# Revit family: LAMP_SHOT LED G2
name_source: partatom
category: Modelos genéricos
revit_build: Autodesk Revit 2015 (Build: 20140606_1530(x64)
units: mm (PartAtom-declared; Revit-internal decimal feet)

## types (20) — shared parameters
CRI = 80
Comentarios de tipo = Availability of tilting between -50º and 230º when placed in a project.
Elevación por defecto = 1219 mm
Fabricante = LAMP
Gear = Electronic
IEE = A+
Installation instructions = https://www.lamp.es
Insulation class = I
Lamp = HIGH POWER LED
Last update = 12/06/2019
MacAdam = 3
Manufacturer URL = http://www.lamp.es
Manufacturer country = Spain
Manufacturer name = LAMP
Model explanation = Availability of tilting between -50º and 230º when placed in a project.
Power Supply = 220-240V 50-60Hz
Product URL = http://www.lamp.es
Product datasheet = http://www.lamp.es
Protection rating = IP65 / IK05
Type = HI POWER NICHIA

## per-type parameters (varying)
| type | Descripción | Efficacy | Finish | Initial color | Initial intensity | LED Lifetime | Luminaire type | Material lira | Modelo | Photometric web file | Plum | Power | Product code | Weight |
| 3850LM 4000 STREET ANT | SHOT G2 5000 STREET 80 NW ANT | 94 lm/W | Textured anthracite grey | 4000 K | 3850 lm | 60.000 L90 B10 | Outdoor - Spotlight | LAMP_Aluminio Shot Antracita | SH250ST840NA | Cabeza Shot g2 : 3850LM 4000 STREET ANT | 41 W | 37 W | SH250ST840NA | 6.43 kg |
| 3850LM 4000 STREET GR | SHOT G2 5000 STREET 80 NW GR | 94 lm/W | Texturised grey | 4000 K | 3850 lm | 60.000 L90 B10 | Outdoor - Spotlight | LAMP_Aluminio Shot | SH250ST840NG | Cabeza Shot g2 : 3850LM 4000 STREET GR | 41 W | 37 W | SH250ST840NG | 6.43 kg |
| 4112LM 3000 MEDIUM FLOOD ANT | SHOT G2 5000 MFL 80 WW ANT | 100 lm/W | Textured anthracite grey | 3000 K | 4112 lm | 60.000 L90 B10 | Outdoor - Spotlight | LAMP_Aluminio Shot Antracita | SH250MF830NA | Cabeza Shot g2 : 4112LM 3000 MEDIUM FLOOD ANT | 41 W | 37 W | SH250MF830NA | 6.38 kg |
| 4112LM 3000 MEDIUM FLOOD GR | SHOT G2 5000 MFL 80 WW GR | 100 lm/W | Texturised grey | 3000 K | 4112 lm | 60.000 L90 B10 | Outdoor - Spotlight | LAMP_Aluminio Shot | SH250MF830NG | Cabeza Shot g2 : 4112LM 3000 MEDIUM FLOOD GR | 41 W | 37 W | SH250MF830NG | 6.38 kg |
| 4112LM 4000 MEDIUM FLOOD ANT | SHOT G2 5000 MFL 80 NW ANT | 100 lm/W | Textured anthracite grey | 4000 K | 4112 lm | 60.000 L90 B10 | Outdoor - Spotlight | LAMP_Aluminio Shot Antracita | SH250MF840NA | Cabeza Shot g2 : 4112LM 4000 MEDIUM FLOOD ANT | 41 W | 37 W | SH250MF840NA | 6.38 kg |
| 4112LM 4000 MEDIUM FLOOD GR | SHOT G2 5000 MFL 80 NW GR | 100 lm/W | Texturised grey | 4000 K | 4112 lm | 60.000 L90 B10 | Outdoor - Spotlight | LAMP_Aluminio Shot | SH250MF840NG | Cabeza Shot g2 : 4112LM 4000 MEDIUM FLOOD GR | 41 W | 37 W | SH250MF840NG | 6.38 kg |
| 4127LM 3000 SPOT ANT | SHOT G2 5000 SP 80 WW ANT | 101 lm/W | Textured anthracite grey | 3000 K | 4127 lm | 60.000 L90 B10 | Outdoor - Spotlight | LAMP_Aluminio Shot Antracita | SH250SP830NA | Cabeza Shot g2 : 4127LM 3000 SPOT ANT | 41 W | 37 W | SH250SP830NA | 6.38 kg |
| 4127LM 3000 SPOT GR | SHOT G2 5000 SP 80 WW GR | 101 lm/W | Texturised grey | 3000 K | 4127 lm | 60.000 L90 B10 | Outdoor - Spotlight | LAMP_Aluminio Shot | SH250SP830NG | Cabeza Shot g2 : 4127LM 3000 SPOT GR | 41 W | 37 W | SH250SP830NG | 6.38 kg |
| 4127LM 4000 SPOT ANT | SHOT G2 5000 SP 80 NW ANT | 101 lm/W | Textured anthracite grey | 4000 K | 4127 lm | 60.000 L90 B10 | Outdoor - Spotlight | LAMP_Aluminio Shot Antracita | SH250SP840NA | Cabeza Shot g2 : 4127LM 4000 SPOT ANT | 41 W | 37 W | SH250SP840NA | 6.38 kg |
| 4127LM 4000 SPOT GR | SHOT G2 5000 SP 80 NW GR | 101 lm/W | Texturised grey | 4000 K | 4127 lm | 60.000 L90 B10 | Outdoor - Spotlight | LAMP_Aluminio Shot | SH250SP840NG | Cabeza Shot g2 : 4127LM 4000 SPOT GR | 41 W | 37 W | SH250SP840NG | 6.38 kg |
| 5050LM 4000 STREET ANT | SHOT G2 7200 STREET 80 NW ANT | 83 lm/W | Textured anthracite grey | 4000 K | 5050 lm | 60.000 L80 B10 | Outdoor - Spotlight | LAMP_Aluminio Shot Antracita | SH270ST840NA | Cabeza Shot g2 : 5050LM 4000 STREET ANT | 61 W | 56 W | SH270ST840NA | 6.52 kg |
| 5050LM 4000 STREET GR | SHOT G2 7200 STREET 80 NW GR | 83 lm/W | Texturised grey | 4000 K | 5050 lm | 60.000 L80 B10 | Outdoor - Spotlight | LAMP_Aluminio Shot | SH270ST840NG | Cabeza Shot g2 : 5050LM 4000 STREET GR | 61 W | 56 W | SH270ST840NG | 6.52 kg |
| 5396LM 3000 MEDIUM FLOOD ANT | SHOT G2 7200 MFL 80 WW ANT | 88 lm/W | Textured anthracite grey | 3000 K | 5396 lm | 60.000 L80 B10 | Outdoor - Spotlight | LAMP_Aluminio Shot Antracita | SH270MF830NA | Cabeza Shot g2 : 5396LM 3000 MEDIUM FLOOD ANT | 61 W | 56 W | SH270MF830NA | 6.47 kg |
| 5396LM 3000 MEDIUM FLOOD GR | SHOT G2 7200 MFL 80 WW GR | 88 lm/W | Texturised grey | 3000 K | 5396 lm | 60.000 L80 B10 | Outdoor - Spotlight | LAMP_Aluminio Shot | SH270MF830NG | Cabeza Shot g2 : 5396LM 3000 MEDIUM FLOOD GR | 61 W | 56 W | SH270MF830NG | 6.47 kg |
| 5396LM 4000 MEDIUM FLOOD ANT | SHOT G2 7200 MFL 80 NW ANT | 88 lm/W | Textured anthracite grey | 4000 K | 5396 lm | 60.000 L80 B10 | Outdoor - Spotlight | LAMP_Aluminio Shot Antracita | SH270MF840NA | Cabeza Shot g2 : 5396LM 4000 MEDIUM FLOOD ANT | 61 W | 56 W | SH270MF840NA | 6.47 kg |
| 5396LM 4000 MEDIUM FLOOD GR | SHOT G2 7200 MFL 80 NW GR | 88 lm/W | Texturised grey | 4000 K | 5396 lm | 60.000 L80 B10 | Outdoor - Spotlight | LAMP_Aluminio Shot | SH270MF840NG | Cabeza Shot g2 : 5396LM 4000 MEDIUM FLOOD GR | 61 W | 56 W | SH270MF840NG | 6.47 kg |
| 5419LM 3000 SPOT ANT | SHOT G2 7200 SP 80 WW ANT | 89 lm/W | Textured anthracite grey | 3000 K | 5419 lm | 60.000 L80 B10 | Outdoor - Spotlight | LAMP_Aluminio Shot Antracita | SH270SP830NA | Cabeza Shot g2 : 5419LM 3000 SPOT ANT | 61 W | 56 W | SH270SP830NA | 6.47 kg |
| 5419LM 3000 SPOT GR | SHOT G2 7200 SP 80 WW GR | 89 lm/W | Texturised grey | 3000 K | 5419 lm | 60.000 L80 B10 | Outdoor - Spotlight | LAMP_Aluminio Shot | SH270SP830NG | Cabeza Shot g2 : 5419LM 3000 SPOT GR | 61 W | 56 W | SH270SP830NG | 6.47 kg |
| 5419LM 4000 SPOT ANT | SHOT G2 7200 SP 80 NW ANT | 89 lm/W | Textured anthracite grey | 4000 K | 5419 lm | 60.000 L80 B10 | Outdoor - Spotlight | LAMP_Aluminio Shot Antracita | SH270SP840NA | Cabeza Shot g2 : 5419LM 4000 SPOT ANT | 61 W | 56 W | SH270SP840NA | 6.47 kg |
| 5419LM 4000 SPOT GR | SHOT G2 7200 SP 80 NW GR | 89 lm/W | Texturised grey | 4000 K | 5419 lm | 60.000 L80 B10 |  | LAMP_Aluminio Shot | SH270SP840NG | Cabeza Shot g2 : 5419LM 4000 SPOT GR | 61 W | 56 W | SH270SP840NG | 6.47 kg |
